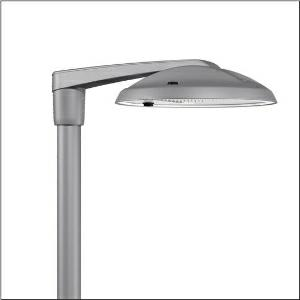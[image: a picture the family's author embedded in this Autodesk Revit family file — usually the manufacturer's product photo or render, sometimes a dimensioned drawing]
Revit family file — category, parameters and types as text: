
# Revit family: dl_r__50_iq_mini___st1_0a_5xa248d31y08me_abd5
name_source: partatom
category: Lighting Fixtures
units: mm (PartAtom-declared; Revit-internal decimal feet)

## family parameters
Cut with Voids When Loaded = No
Host = Face
Light Source = No
Part Type = Normal
Room Calculation Point = No
Round Connector Dimension = Use Diameter
Shared = No

## types (1)
- --- (1 x LED, 15720 lm, 107 W, 3000K)
    Apparent Load = 107 VA
    CIE Flux Codes = 37 72 97 100 100
    Color Rendering = 70
    Color Temperature = 3000K
    Default Elevation = 1800 mm
    Description = DL® 50 iQ mini, mast luminaire, primary light control with lens, of PMMA, primary optical cover: cover, of toughened safety glass, transparent, light distribution: ST1.0a, light emission: direct distribution, primary light characteristic: asymmetric, installation type: post-top, side-entry, LED, High Power LED, rated luminous flux: 15.720lm, luminous efficacy: 147lm/W, light colour: 730, colour temperature: 3000K, control gear: iQ-Street Remote, D4i with power reduction, control: optimised constant luminous flux control (CLO 2.0), Desk-Remote (wireless, voltage-free reading and setting of iQ features in the workshop via application-optimized NFC function/RFID function), Light-Fading, Smart-Wire, Night-Set, Lumen-Switch, Temp-Guard, Auto-Match, Street-Remote, pre-setting: logarithmic dimming characteristic, mains connection: 230..240V, AC, 50/60Hz, connection cable pre-assembled, cable length: 10,5m, start of lifetime: 107W, end of service life: 113W, reduction: 47W, luminaire housing, of diecast aluminium, powder-coated, Siteco® metallic grey (DB 702S), inclination adjustable: 0°, 5°, 10° (post-top) | 0°, -5°, -10°, -15° (side-entry), please order mast post-top element or mast side-entry element separately, diameter: 500mm, height: 115mm, post-top: for spigot size d x l = 76 x 100mm; with reducer (optional accessory) 60 x 100mm | side-entry: for spigot size d x l = 60 x 100mm; with reducer (optional accessory) 42 x 100mm, mounting height: 4..6m, Smart Interface below and above, protection rating (complete): IP66, insulation class (complete): insulation class II (safety insulation), certification: CE, ENEC, ENEC+, VDE, impact resistance: IK08, permissible operating ambient temperature for outdoor applications: -25..+40°C, standard-compliant lighting for roads and squares, packaging unit: 1 piece

Light Distribution: ST1.0a
    Height = 115 mm
    Lamp = 1 x LED
    Lamp Light Flux = 15720 lm
    Lamp Power = 107 W
    Lamp count = 1
    Length = 500 mm
    Luminous efficacy = 147 lm/W
    Manufacturer = Siteco
    ModVariant = No
    Model = 5XA248D31Y08ME
    Number of Poles = 1
    OnlyDefault = Yes
    Power Factor = 1
    Product Name = DL® 50 iQ mini | ST1.0a
    Product group = mast luminaire | pylon top
    ProductGroupID = 6100
    Protection Class = Protection class II
    Protection Degree = IP 66
    RLX_Detail_Level = 1
    RLX_Emergency_Light_Flux = 0 lm
    RLX_Emergency_Type = 0
    RLX_Emergency_Type_DB = No
    RlxData = <blob elided: 106649 chars, md5=217556e8>
    Socket = socket
    Standby Power = 0 W
    System Light Flux = 15720 lm
    System Power = 107 W
    Type Comments = factory setting: luminous flux: 100 % | dim-lin: 254 | 565 mA
    Type Image = l_1251786.jpg
    URL = http://relux.com
    VarID = @adj_086775
    Voltage = 0 V
    Weight = 0.00 kg
    Width = 0 mm  [stored 0 ft]

note: [stored X ft] marks values corroborated as IEEE doubles in the binary element streams (Revit-internal decimal feet)

## geometry (parser evidence)
native form markers: Blend x4, Sweep x9
no freeform markers — native parametric forms only
